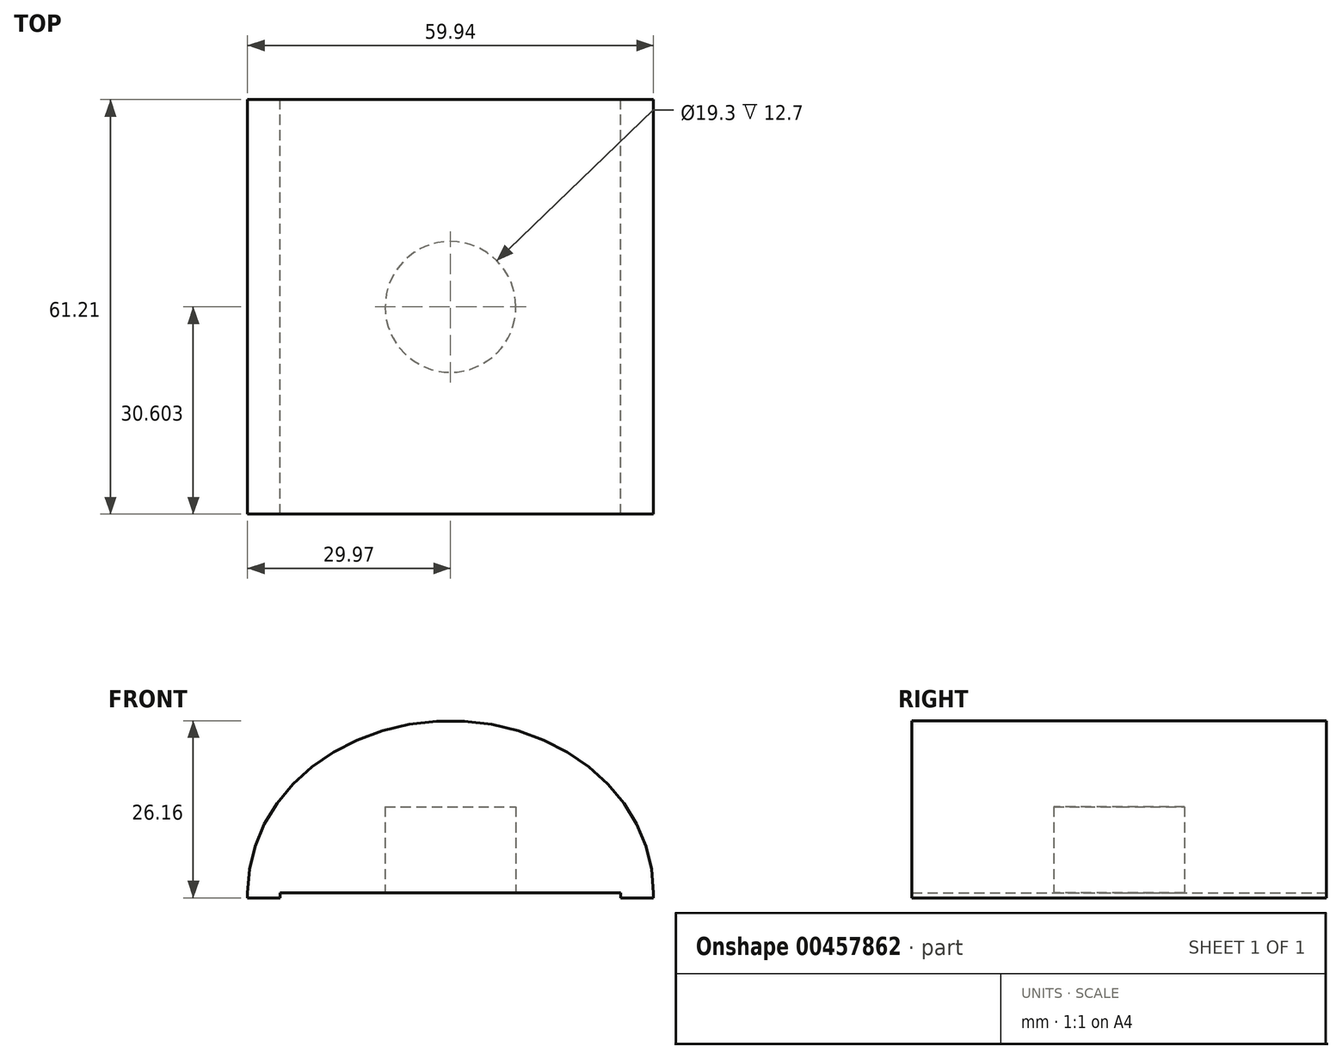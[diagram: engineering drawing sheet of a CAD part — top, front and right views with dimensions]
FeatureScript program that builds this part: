
annotation { "Feature Type Name" : "Feature", "Feature Type Description" : "" }
export const myFeature = defineFeature(function(context is Context, id is Id, definition is map)
    precondition{}
    {
        {
            var Q0;
            Q0=qCreatedBy(makeId("Front.planeOp"),FACE);
            var sketch = newSketch(context, id + "F0", { "sketchPlane" : qUnion([Q0])});
            skLineSegment(sketch, "E0.bottom", {"start": v(-24.04, -16.6) * mm, "end": v(35.9, -16.6) * mm});
            skEllipticalArc(sketch, "E1", {});
            const initialGuessF0  = {"E1": [0.005930390208959578, -0.016592934209376707, -1, 0, 0.029972, 0.0254, 3.141592653589793, 0]};
            skSetInitialGuess(sketch, initialGuessF0);
            skSolve(sketch);
        }
        {
            var Q0;
            Q0=makeQuery(id+"F0.imprint","IMPRINT",FACE,{"disambiguationData":[TD([[makeQuery(id+"F0.imprint","IMPRINT",EDGE,{"derivedFrom":sQuery(id+"F0.wireOp",EDGE,"E0.bottom")}),1.0]])]});
            extrude(context, id + "F1", {"entities" : qUnion([Q0]), "depth" : 61.2 * mm});
        }
        {
            var Q0;
            Q0=makeQuery(id+"F1.opExtrude","SWEPT_FACE",FACE,{"disambiguationData":[OSD([sQuery(id+"F0.wireOp",EDGE,"E0.bottom")])]});
            var sketch = newSketch(context, id + "F2", { "sketchPlane" : qUnion([Q0])});
            skLineSegment(sketch, "E2", {"start": v(-24.04, 61.21) * mm, "end": v(-24.04, 61.21) * mm});
            skLineSegment(sketch, "E3", {"start": v(-24.04, 61.21) * mm, "end": v(-19.22, 61.21) * mm});
            skLineSegment(sketch, "E4", {"start": v(-19.22, 61.21) * mm, "end": v(-19.22, 0) * mm});
            skLineSegment(sketch, "E5", {"start": v(35.9, 61.21) * mm, "end": v(31.08, 61.21) * mm});
            skLineSegment(sketch, "E6", {"start": v(31.08, 61.21) * mm, "end": v(31.08, 0) * mm});
            skSolve(sketch);
        }
        {
            var Q0;
            Q0=makeQuery(id+"F2.imprint","IMPRINT",FACE,{"disambiguationData":[TD([[makeQuery(id+"F2.imprint","IMPRINT",EDGE,{"derivedFrom":sQuery(id+"F2.wireOp",EDGE,"E3")}),-1.0]])]});
            var Q1;
            Q1=makeQuery(id+"F2.imprint","IMPRINT",FACE,{"disambiguationData":[TD([[makeQuery(id+"F2.imprint","IMPRINT",EDGE,{"derivedFrom":sQuery(id+"F2.wireOp",EDGE,"E5")}),-1.0]])]});
            extrude(context, id + "F3", {"entities" : qUnion([Q0, Q1]), "operationType" : NewBodyOperationType.ADD, "depth" : 0.76 * mm});
        }
        {
            var Q0;
            Q0=makeQuery(id+"F1.opExtrude","SWEPT_FACE",FACE,{"disambiguationData":[OSD([sQuery(id+"F0.wireOp",EDGE,"E0.bottom")])]});
            var sketch = newSketch(context, id + "F4", { "sketchPlane" : qUnion([Q0])});
            skCircle(sketch, "E7", {"center": v(5.93, 30.6) * mm, "radius": 9.65 * mm});
            skPoint(sketch, "E8.orphan", {"position": v(-19.22, 30.6) * mm});
            skPoint(sketch, "E9.orphan", {"position": v(5.93, 61.21) * mm});
            skPoint(sketch, "E10.end.orphan", {"position": v(31.08, 30.6) * mm});
            skPoint(sketch, "E11.end.orphan", {"position": v(5.93, 0) * mm});
            skSolve(sketch);
        }
        {
            var Q0;
            Q0=makeQuery(id+"F4.imprint","IMPRINT",FACE,{"disambiguationData":[TD([[makeQuery(id+"F4.imprint","IMPRINT",EDGE,{"derivedFrom":sQuery(id+"F4.wireOp",EDGE,"E7")}),1.0]])]});
            extrude(context, id + "F5", {"entities" : qUnion([Q0]), "operationType" : NewBodyOperationType.REMOVE, "oppositeDirection" : true, "depth" : 12.7 * mm});
        }
    });
